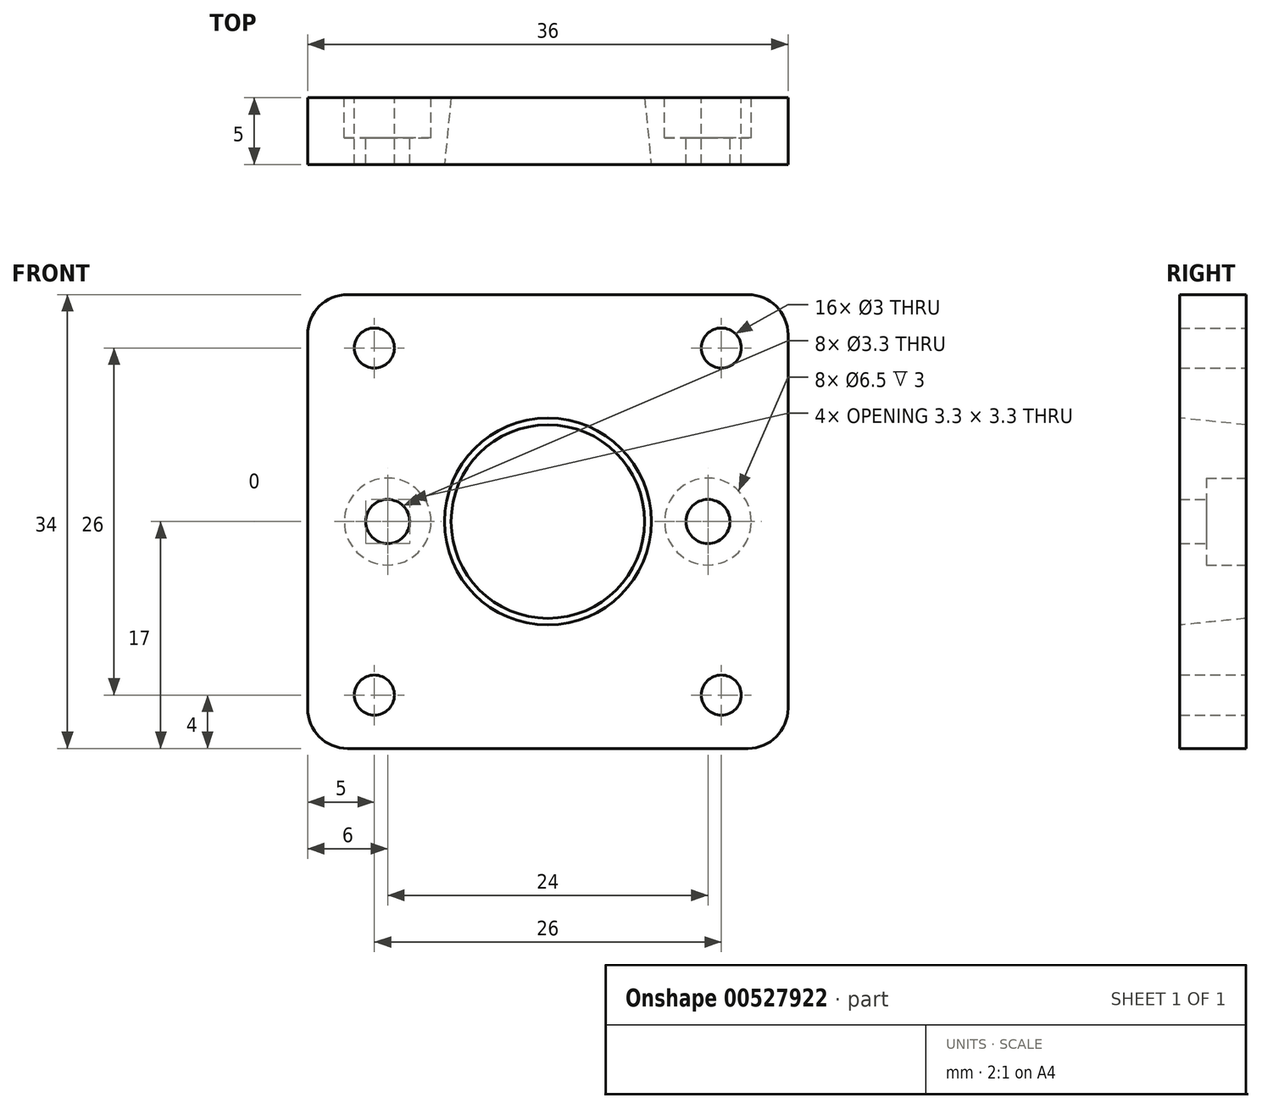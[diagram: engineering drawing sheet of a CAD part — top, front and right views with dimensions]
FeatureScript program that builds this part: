
annotation { "Feature Type Name" : "Feature", "Feature Type Description" : "" }
export const myFeature = defineFeature(function(context is Context, id is Id, definition is map)
    precondition{}
    {
        {
            var Q0;
            Q0=qCreatedBy(makeId("Front.planeOp"),FACE);
            var sketch = newSketch(context, id + "F0", { "sketchPlane" : qUnion([Q0])});
            skLineSegment(sketch, "E0.bottom", {"start": v(18, -17) * mm, "end": v(-18, -17) * mm});
            skLineSegment(sketch, "E0.top", {"start": v(18, 17) * mm, "end": v(-18, 17) * mm});
            skLineSegment(sketch, "E0.left", {"start": v(18, -17) * mm, "end": v(18, 17) * mm});
            skLineSegment(sketch, "E0.right", {"start": v(-18, -17) * mm, "end": v(-18, 17) * mm});
            skPoint(sketch, "E0.middle", {"position": v(0, 0) * mm});
            skCircle(sketch, "E1", {"center": v(-13, 13) * mm, "radius": 1.5 * mm});
            skCircle(sketch, "E2.MirrorC", {"center": v(13, 13) * mm, "radius": 1.5 * mm});
            skCircle(sketch, "E3.MirrorC", {"center": v(-13, -13) * mm, "radius": 1.5 * mm});
            skCircle(sketch, "E4.MirrorC", {"center": v(13, -13) * mm, "radius": 1.5 * mm});
            skCircle(sketch, "E5", {"center": v(0, 0) * mm, "radius": 7.25 * mm});
            skPoint(sketch, "E6", {"position": v(12, 0) * mm});
            skPoint(sketch, "E7", {"position": v(-12, 0) * mm});
            skPoint(sketch, "E8.centerSnap0", {"position": v(0, 17) * mm});
            skSolve(sketch);
        }
        {
            var Q0;
            {var subQ0=sQuery(id+"F0.wireOp",EDGE,"E0.right");Q0=makeQuery(id+"F0.imprint","IMPRINT",FACE,{"disambiguationData":[TD([[makeQuery(id+"F0.imprint","IMPRINT",EDGE,{"derivedFrom":subQ0}),-1.0]])]});}
            extrude(context, id + "F1", {"entities" : qUnion([Q0]), "depth" : 5 * mm, "offsetDistance" : 25 * mm});
        }
        {
            var Q0;
            Q0=makeQuery(id+"F1.opExtrude","SWEPT_EDGE",EDGE,{"disambiguationData":[OSD([sQuery(id+"F0.wireOp",EDGE,"E0.top"),sQuery(id+"F0.wireOp",EDGE,"E0.right")])]});
            var Q1;
            Q1=makeQuery(id+"F1.opExtrude","SWEPT_EDGE",EDGE,{"disambiguationData":[OSD([sQuery(id+"F0.wireOp",EDGE,"E0.top"),sQuery(id+"F0.wireOp",EDGE,"E0.left")])]});
            var Q2;
            Q2=makeQuery(id+"F1.opExtrude","SWEPT_EDGE",EDGE,{"disambiguationData":[OSD([sQuery(id+"F0.wireOp",EDGE,"E0.bottom"),sQuery(id+"F0.wireOp",EDGE,"E0.left")])]});
            var Q3;
            Q3=makeQuery(id+"F1.opExtrude","SWEPT_EDGE",EDGE,{"disambiguationData":[OSD([sQuery(id+"F0.wireOp",EDGE,"E0.bottom"),sQuery(id+"F0.wireOp",EDGE,"E0.right")])]});
            fillet(context, id + "F2", {"entities" : qUnion([Q0, Q1, Q2, Q3]), "radius" : 3 * mm, "tangentPropagation" : true, "allowEdgeOverflow" : false});
        }
        {
            var Q0;
            Q0=makeQuery(id+"F1.opExtrude","CAP_EDGE",EDGE,{"disambiguationData":[OSD([sQuery(id+"F0.wireOp",EDGE,"E5")])],"isStart":false});
            chamfer(context, id + "F3", {"entities" : qUnion([Q0]), "chamferType" : ChamferType.TWO_OFFSETS, "width1" : 0.5 * mm, "oppositeDirection" : true, "width2" : 5 * mm, "tangentPropagation" : true});
        }
        {
            var Q0;
            Q0=sQuery(id+"F0.wireOp",VERTEX,"E6");
            var Q1;
            Q1=sQuery(id+"F0.wireOp",VERTEX,"E7");
            var Q2;
            Q2=makeQuery(id+"F1.opExtrude","SWEPT_BODY",BODY,{"disambiguationData":[OSD([sQuery(id+"F0.wireOp",EDGE,"E0.bottom"),sQuery(id+"F0.wireOp",EDGE,"E0.top"),sQuery(id+"F0.wireOp",EDGE,"E0.left"),sQuery(id+"F0.wireOp",EDGE,"E0.right"),sQuery(id+"F0.wireOp",EDGE,"E1"),sQuery(id+"F0.wireOp",EDGE,"E2.MirrorC"),sQuery(id+"F0.wireOp",EDGE,"E3.MirrorC"),sQuery(id+"F0.wireOp",EDGE,"E4.MirrorC"),sQuery(id+"F0.wireOp",EDGE,"E5")])]});
            hole(context, id + "F4", {"style" : HoleStyle.C_BORE, "endStyle" : HoleEndStyle.THROUGH, "oppositeDirection" : true, "standardTappedOrClearance" : lookupTablePath({ "standard" : "ISO", "fit" : "Normal", "size" : "M3", "type" : "Clearance" }), "standardBlindInLast" : lookupTablePath({ "fit" : "Standard", "standard" : "ISO", "size" : "M3", "type" : "Clearance" }), "holeDiameter" : 3.3 * mm, "cBoreDiameter" : 6.5 * mm, "cBoreDepth" : 3 * mm, "isTappedThrough" : true, "tappedDepth" : 12 * mm, "tapClearance" : 3, "locations" : qUnion([Q0, Q1]), "scope" : qUnion([Q2])});
        }
    });
